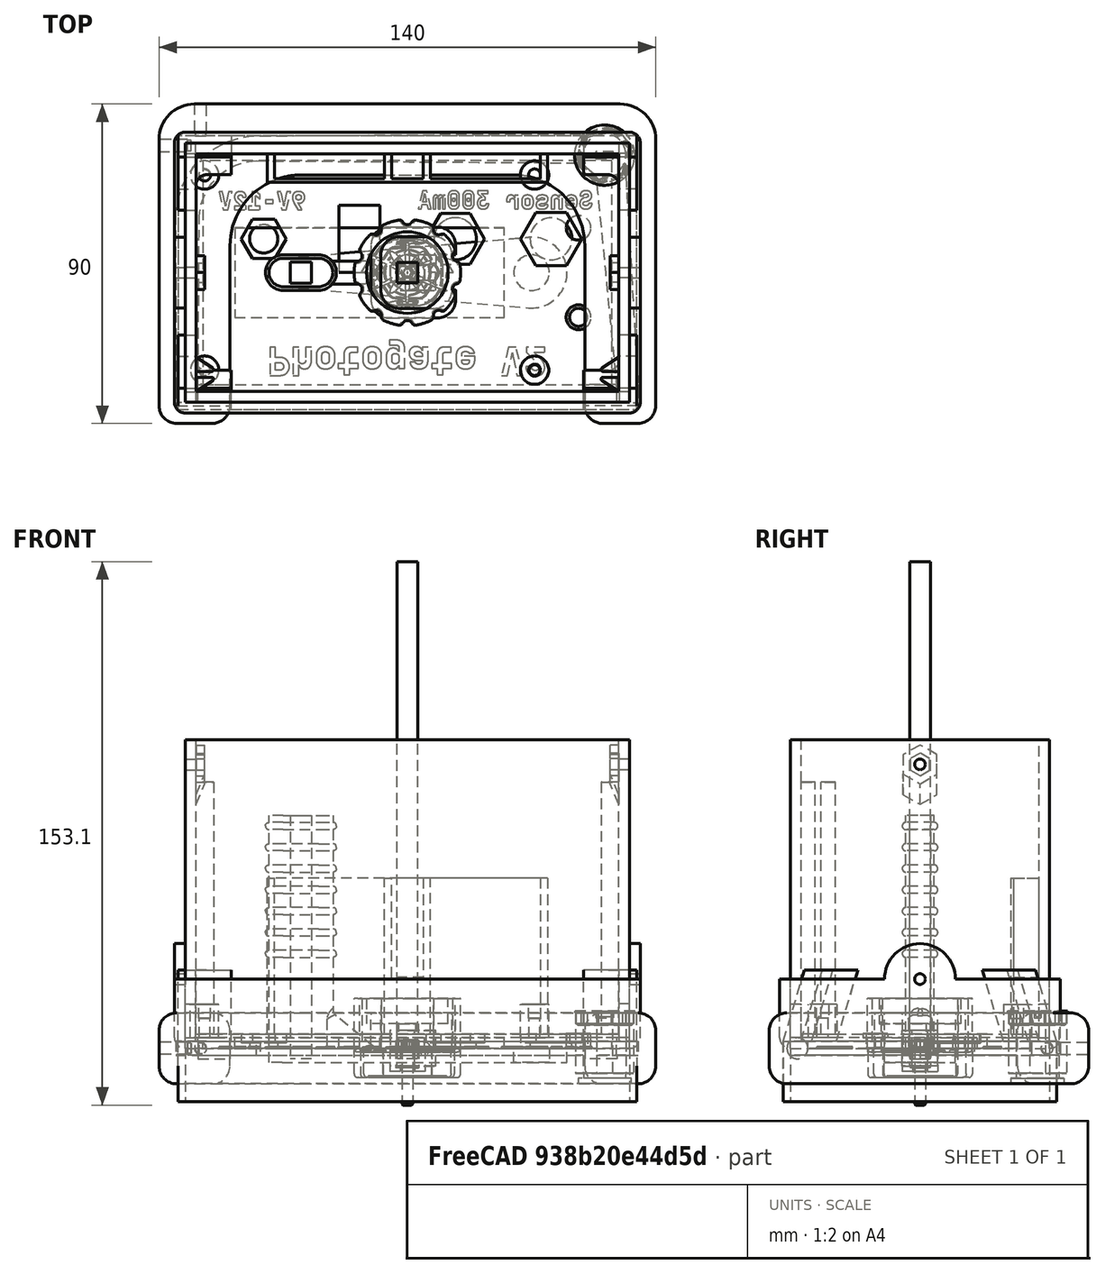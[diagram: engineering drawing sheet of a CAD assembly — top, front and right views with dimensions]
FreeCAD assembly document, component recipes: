
FREECAD ASSEMBLY — COMPONENT RECIPES ("All_Models")

This assembly document has 21 components, labeled P0..P20 below (a component is one placed body or linked part). 17 of them carry a construction recipe — the FreeCAD feature program that regenerates the part from scratch, quoted from this document or its linked companion documents; the rest are supplied as boundary geometry only. No exploded tour is included for this assembly.
NOTE — document 2 of 2 of this assembly tour. The two overview renders and the header above are repeated from document 1; the component sections below continue where the previous document stopped.
COMPONENT P18 — recipe-attached ("ThumbScrew001", modeled in this document).
Construction recipe (the document's own serialized feature program — sketch geometry with constraints, then the solid features built on it; lengths are millimeters unless a unit is written):

FEATURE [Sketcher::SketchObject] Sketch012
  ArcFitTolerance = 1e-06
  AttachmentSupport = -> [XY_Plane003]
  ExternalTypes = [0]
  FullyConstrained = true
  MakeInternals = false
  MapMode = 5
  _ExternalGeoVersion = 0
  sketch-geometry (1):
    g0: Circle CenterX=0 CenterY=0 CenterZ=0 NormalX=0 NormalY=0 NormalZ=1 AngleXU=0 Radius=15
  constraints (2):
    c: Diameter(g0) = 30
    c: Coincident(g0,g-1)
FEATURE [PartDesign::Pad] Pad012
  Direction = (0,0,1)
  Length = 8.2
  Length2 = 10
  Profile = -> Sketch012
  ReferenceAxis = -> Sketch012 [N_Axis]
  Refine = true
  Reversed = true
  SideType = 0
  Suppressed = false
  Type = 0
  Type2 = 0
FEATURE [Sketcher::SketchObject] Sketch013
  ArcFitTolerance = 1e-06
  AttachmentSupport = -> [XY_Plane003]
  ExternalGeometry = -> [Pad012]
  ExternalTypes = [0]
  FullyConstrained = true
  MakeInternals = false
  MapMode = 5
  _ExternalGeoVersion = 0
  sketch-geometry (4):
    g0: LineSegment [constr] StartX=0 StartY=0 StartZ=0 EndX=-1.95789 EndY=14.8717 EndZ=0
    g1: LineSegment [constr] StartX=0 StartY=0 StartZ=0 EndX=1.95789 EndY=14.8717 EndZ=0
    g2: ArcOfCircle CenterX=0 CenterY=0 CenterZ=0 NormalX=0 NormalY=0 NormalZ=1 AngleXU=0 Radius=15 StartAngle=1.4399 EndAngle=1.7017
    g3: ArcOfCircle CenterX=-4.3e-15 CenterY=15 CenterZ=0 NormalX=0 NormalY=0 NormalZ=1 AngleXU=0 Radius=1.96209 StartAngle=3.20704 EndAngle=6.21774
  constraints (12):
    c: PointOnObject(g0,g-3)
    c: PointOnObject(g1,g-3)
    c: Horizontal(g1,g0)
    c: Coincident(g1,g-1)
    c: Coincident(g0,g1)
    c: PointOnObject(g3,g2)
    c: Coincident(g3,g2)
    c: Coincident(g3,g2)
    c: Coincident(g2,g0)
    c: Horizontal(g0,g2)
    c: Coincident(g2,g0)
    c: Angle(g1,g0) = 0.261799
FEATURE [PartDesign::Pocket] Pocket011
  BaseFeature = -> Pad012
  Direction = (0,0,-1)
  Length = 5
  Length2 = 5
  Profile = -> Sketch013
  ReferenceAxis = -> Sketch013 [N_Axis]
  Refine = true
  SideType = 0
  Suppressed = false
  Type = 1
  Type2 = 0
FEATURE [PartDesign::PolarPattern] PolarPattern
  Angle = 360
  Axis = -> Sketch013 [N_Axis]
  BaseFeature = -> Pocket011
  Mode = 0
  Occurrences = 10
  Offset = 120
  Originals = -> [Pocket011]
  Refine = true
  SpacingPattern = [0]
  Spacings = [-1,-1,-1,-1,-1,-1,-1,-1,-1]
  Suppressed = false
  TransformMode = 0
FEATURE [PartDesign::Fillet] Fillet002
  Base = -> PolarPattern [Face22,Face11,Face9,Face7,Face5,Face3,Face21,Face19,Face17,Face15,Face13]
  BaseFeature = -> PolarPattern
  Radius = 1
  Refine = true
  SupportTransform = false
  Suppressed = false
  UseAllEdges = false
FEATURE [Sketcher::SketchObject] Sketch015
  ArcFitTolerance = 1e-06
  AttachmentSupport = -> [Fillet002]
  ExternalTypes = [0]
  FullyConstrained = true
  MakeInternals = false
  MapMode = 5
  _ExternalGeoVersion = 0
  sketch-geometry (9):
    g0: Circle CenterX=0 CenterY=0 CenterZ=0 NormalX=0 NormalY=0 NormalZ=1 AngleXU=0 Radius=4.85
    g1: Circle CenterX=0 CenterY=0 CenterZ=0 NormalX=0 NormalY=0 NormalZ=1 AngleXU=0 Radius=2.75
    g2: LineSegment StartX=2.6 StartY=1.50111 StartZ=0 EndX=4.237e-13 EndY=3.00222 EndZ=0
    g3: LineSegment StartX=4.237e-13 StartY=3.00222 StartZ=0 EndX=-2.6 EndY=1.50111 EndZ=0
    g4: LineSegment StartX=-2.6 StartY=1.50111 StartZ=0 EndX=-2.6 EndY=-1.50111 EndZ=0
    g5: LineSegment StartX=-2.6 StartY=-1.50111 StartZ=0 EndX=1.88329e-11 EndY=-3.00222 EndZ=0
    g6: LineSegment StartX=1.88329e-11 StartY=-3.00222 StartZ=0 EndX=2.6 EndY=-1.50111 EndZ=0
    g7: LineSegment StartX=2.6 StartY=-1.50111 StartZ=0 EndX=2.6 EndY=1.50111 EndZ=0
    g8: Circle [constr] CenterX=0 CenterY=0 CenterZ=0 NormalX=0 NormalY=0 NormalZ=1 AngleXU=0 Radius=3.00222
  constraints (20):
    c: Diameter(g0) = 9.7
    c: Coincident(g0,g-1)
    c: Diameter(g1) = 5.5
    c: Coincident(g1,g0)
    c: Coincident(g2,g3)
    c: Coincident(g3,g4)
    c: Coincident(g4,g5)
    c: Coincident(g5,g6)
    c: Coincident(g6,g7)
    c: Coincident(g7,g2)
    c: Equal(g2, g3-g7) x5
    c: PointOnObject(g2,g8)
    c: PointOnObject(g3,g8)
    c: PointOnObject(g4,g8)
    c: PointOnObject(g5,g8)
    c: PointOnObject(g6,g8)
    c: PointOnObject(g7,g8)
    c: Coincident(g8,g0)
    c: Horizontal(g3,g2)
    c: DistanceX(g3,g2) = 5.2
FEATURE [PartDesign::Pocket] Pocket012
  BaseFeature = -> Fillet002
  Direction = (0,0,-1)
  Length = 3
  Length2 = 5
  Profile = -> Sketch015 [Edge2]
  ReferenceAxis = -> Sketch015 [N_Axis]
  Refine = true
  SideType = 0
  Suppressed = false
  Type = 0
  Type2 = 0
FEATURE [PartDesign::Pad] Pad032
  BaseFeature = -> Pocket012
  Direction = (0,0,1)
  Length = 4
  Length2 = 10
  Profile = -> Sketch015 [Edge1,Edge6,Edge5,Edge7,Edge8,Edge3,Edge4]
  ReferenceAxis = -> Sketch015 [N_Axis]
  Refine = true
  SideType = 0
  Suppressed = false
  Type = 0
  Type2 = 0
FEATURE [Sketcher::SketchObject] Sketch050  label="LorxiSymbol"
  ArcFitTolerance = 1e-06
  AttachmentOffset = pos=(11,-9.424,0) rot=(0,0,1;0rad)
  AttachmentSupport = -> [Pad032]
  ExternalTypes = [0]
  FullyConstrained = false
  MakeInternals = false
  MapMode = 5
  Placement = pos=(11,9.424,-8.2) rot=(1,0,0;3.14159rad)
  _ExternalGeoVersion = 0
  sketch-geometry (292):
    g0: BSplineCurve PolesCount=4 KnotsCount=2 Degree=3 IsPeriodic=0
    g1: BSplineCurve PolesCount=2 KnotsCount=2 Degree=1 IsPeriodic=0
    g2: BSplineCurve PolesCount=2 KnotsCount=2 Degree=1 IsPeriodic=0
    g3: BSplineCurve PolesCount=2 KnotsCount=2 Degree=1 IsPeriodic=0
    g4: BSplineCurve PolesCount=4 KnotsCount=2 Degree=3 IsPeriodic=0
    g5: BSplineCurve PolesCount=4 KnotsCount=2 Degree=3 IsPeriodic=0
    g6: BSplineCurve PolesCount=2 KnotsCount=2 Degree=1 IsPeriodic=0
    g7: BSplineCurve PolesCount=2 KnotsCount=2 Degree=1 IsPeriodic=0
    g8: BSplineCurve PolesCount=2 KnotsCount=2 Degree=1 IsPeriodic=0
    g9: BSplineCurve PolesCount=4 KnotsCount=2 Degree=3 IsPeriodic=0
    g10: BSplineCurve PolesCount=2 KnotsCount=2 Degree=1 IsPeriodic=0
    g11: BSplineCurve PolesCount=2 KnotsCount=2 Degree=1 IsPeriodic=0
    g12: BSplineCurve PolesCount=4 KnotsCount=2 Degree=3 IsPeriodic=0
    g13: BSplineCurve PolesCount=4 KnotsCount=2 Degree=3 IsPeriodic=0
    g14: BSplineCurve PolesCount=2 KnotsCount=2 Degree=1 IsPeriodic=0
    g15: BSplineCurve PolesCount=2 KnotsCount=2 Degree=1 IsPeriodic=0
    g16: BSplineCurve PolesCount=2 KnotsCount=2 Degree=1 IsPeriodic=0
    g17: BSplineCurve PolesCount=4 KnotsCount=2 Degree=3 IsPeriodic=0
    g18: BSplineCurve PolesCount=2 KnotsCount=2 Degree=1 IsPeriodic=0
    g19: BSplineCurve PolesCount=4 KnotsCount=2 Degree=3 IsPeriodic=0
    g20: BSplineCurve PolesCount=4 KnotsCount=2 Degree=3 IsPeriodic=0
    g21: BSplineCurve PolesCount=2 KnotsCount=2 Degree=1 IsPeriodic=0
    g22: BSplineCurve PolesCount=4 KnotsCount=2 Degree=3 IsPeriodic=0
    g23: BSplineCurve PolesCount=4 KnotsCount=2 Degree=3 IsPeriodic=0
    g24: BSplineCurve PolesCount=2 KnotsCount=2 Degree=1 IsPeriodic=0
    g25: BSplineCurve PolesCount=4 KnotsCount=2 Degree=3 IsPeriodic=0
    g26: BSplineCurve PolesCount=4 KnotsCount=2 Degree=3 IsPeriodic=0
    g27: BSplineCurve PolesCount=2 KnotsCount=2 Degree=1 IsPeriodic=0
    g28: BSplineCurve PolesCount=4 KnotsCount=2 Degree=3 IsPeriodic=0
    g29: BSplineCurve PolesCount=4 KnotsCount=2 Degree=3 IsPeriodic=0
    g30: BSplineCurve PolesCount=2 KnotsCount=2 Degree=1 IsPeriodic=0
    g31: BSplineCurve PolesCount=4 KnotsCount=2 Degree=3 IsPeriodic=0
    g32: BSplineCurve PolesCount=4 KnotsCount=2 Degree=3 IsPeriodic=0
    g33: BSplineCurve PolesCount=2 KnotsCount=2 Degree=1 IsPeriodic=0
    g34: BSplineCurve PolesCount=4 KnotsCount=2 Degree=3 IsPeriodic=0
    g35: BSplineCurve PolesCount=4 KnotsCount=2 Degree=3 IsPeriodic=0
    g36: BSplineCurve PolesCount=2 KnotsCount=2 Degree=1 IsPeriodic=0
    g37: BSplineCurve PolesCount=4 KnotsCount=2 Degree=3 IsPeriodic=0
    g38: BSplineCurve PolesCount=4 KnotsCount=2 Degree=3 IsPeriodic=0
    g39: BSplineCurve PolesCount=4 KnotsCount=2 Degree=3 IsPeriodic=0
    g40: BSplineCurve PolesCount=4 KnotsCount=2 Degree=3 IsPeriodic=0
    g41: BSplineCurve PolesCount=2 KnotsCount=2 Degree=1 IsPeriodic=0
    g42: BSplineCurve PolesCount=4 KnotsCount=2 Degree=3 IsPeriodic=0
    g43: BSplineCurve PolesCount=4 KnotsCount=2 Degree=3 IsPeriodic=0
    g44: BSplineCurve PolesCount=4 KnotsCount=2 Degree=3 IsPeriodic=0
    g45: BSplineCurve PolesCount=4 KnotsCount=2 Degree=3 IsPeriodic=0
    g46: BSplineCurve PolesCount=2 KnotsCount=2 Degree=1 IsPeriodic=0
    g47: BSplineCurve PolesCount=4 KnotsCount=2 Degree=3 IsPeriodic=0
    g48: BSplineCurve PolesCount=4 KnotsCount=2 Degree=3 IsPeriodic=0
    g49: BSplineCurve PolesCount=4 KnotsCount=2 Degree=3 IsPeriodic=0
    g50: BSplineCurve PolesCount=2 KnotsCount=2 Degree=1 IsPeriodic=0
    g51: BSplineCurve PolesCount=2 KnotsCount=2 Degree=1 IsPeriodic=0
    g52: BSplineCurve PolesCount=4 KnotsCount=2 Degree=3 IsPeriodic=0
    g53: BSplineCurve PolesCount=2 KnotsCount=2 Degree=1 IsPeriodic=0
    g54: BSplineCurve PolesCount=2 KnotsCount=2 Degree=1 IsPeriodic=0
    g55: BSplineCurve PolesCount=2 KnotsCount=2 Degree=1 IsPeriodic=0
    g56: BSplineCurve PolesCount=4 KnotsCount=2 Degree=3 IsPeriodic=0
    g57: BSplineCurve PolesCount=2 KnotsCount=2 Degree=1 IsPeriodic=0
    g58: BSplineCurve PolesCount=2 KnotsCount=2 Degree=1 IsPeriodic=0
    g59: BSplineCurve PolesCount=4 KnotsCount=2 Degree=3 IsPeriodic=0
    g60: BSplineCurve PolesCount=4 KnotsCount=2 Degree=3 IsPeriodic=0
    g61: BSplineCurve PolesCount=4 KnotsCount=2 Degree=3 IsPeriodic=0
    g62: BSplineCurve PolesCount=4 KnotsCount=2 Degree=3 IsPeriodic=0
    g63: BSplineCurve PolesCount=4 KnotsCount=2 Degree=3 IsPeriodic=0
    g64: BSplineCurve PolesCount=4 KnotsCount=2 Degree=3 IsPeriodic=0
    g65: BSplineCurve PolesCount=2 KnotsCount=2 Degree=1 IsPeriodic=0
    g66: BSplineCurve PolesCount=4 KnotsCount=2 Degree=3 IsPeriodic=0
    g67: BSplineCurve PolesCount=4 KnotsCount=2 Degree=3 IsPeriodic=0
    g68: BSplineCurve PolesCount=2 KnotsCount=2 Degree=1 IsPeriodic=0
    g69: BSplineCurve PolesCount=4 KnotsCount=2 Degree=3 IsPeriodic=0
    g70: BSplineCurve PolesCount=4 KnotsCount=2 Degree=3 IsPeriodic=0
    g71: BSplineCurve PolesCount=4 KnotsCount=2 Degree=3 IsPeriodic=0
    g72: BSplineCurve PolesCount=4 KnotsCount=2 Degree=3 IsPeriodic=0
    g73: BSplineCurve PolesCount=4 KnotsCount=2 Degree=3 IsPeriodic=0
    g74: BSplineCurve PolesCount=2 KnotsCount=2 Degree=1 IsPeriodic=0
    g75: BSplineCurve PolesCount=2 KnotsCount=2 Degree=1 IsPeriodic=0
    g76: BSplineCurve PolesCount=4 KnotsCount=2 Degree=3 IsPeriodic=0
    g77: BSplineCurve PolesCount=4 KnotsCount=2 Degree=3 IsPeriodic=0
    g78: BSplineCurve PolesCount=4 KnotsCount=2 Degree=3 IsPeriodic=0
    g79: BSplineCurve PolesCount=4 KnotsCount=2 Degree=3 IsPeriodic=0
    g80: BSplineCurve PolesCount=4 KnotsCount=2 Degree=3 IsPeriodic=0
    g81: BSplineCurve PolesCount=2 KnotsCount=2 Degree=1 IsPeriodic=0
    g82: BSplineCurve PolesCount=4 KnotsCount=2 Degree=3 IsPeriodic=0
    g83: BSplineCurve PolesCount=4 KnotsCount=2 Degree=3 IsPeriodic=0
    g84: BSplineCurve PolesCount=2 KnotsCount=2 Degree=1 IsPeriodic=0
    g85: BSplineCurve PolesCount=4 KnotsCount=2 Degree=3 IsPeriodic=0
    g86: BSplineCurve PolesCount=4 KnotsCount=2 Degree=3 IsPeriodic=0
    g87: BSplineCurve PolesCount=4 KnotsCount=2 Degree=3 IsPeriodic=0
    g88: BSplineCurve PolesCount=4 KnotsCount=2 Degree=3 IsPeriodic=0
    g89: BSplineCurve PolesCount=4 KnotsCount=2 Degree=3 IsPeriodic=0
    g90: BSplineCurve PolesCount=4 KnotsCount=2 Degree=3 IsPeriodic=0
    g91: BSplineCurve PolesCount=2 KnotsCount=2 Degree=1 IsPeriodic=0
    g92: BSplineCurve PolesCount=2 KnotsCount=2 Degree=1 IsPeriodic=0
    g93: BSplineCurve PolesCount=4 KnotsCount=2 Degree=3 IsPeriodic=0
    g94: BSplineCurve PolesCount=2 KnotsCount=2 Degree=1 IsPeriodic=0
    g95: BSplineCurve PolesCount=2 KnotsCount=2 Degree=1 IsPeriodic=0
    g96: BSplineCurve PolesCount=2 KnotsCount=2 Degree=1 IsPeriodic=0
    g97: BSplineCurve PolesCount=4 KnotsCount=2 Degree=3 IsPeriodic=0
    g98: BSplineCurve PolesCount=2 KnotsCount=2 Degree=1 IsPeriodic=0
    g99: BSplineCurve PolesCount=2 KnotsCount=2 Degree=1 IsPeriodic=0
    g100: BSplineCurve PolesCount=4 KnotsCount=2 Degree=3 IsPeriodic=0
    g101: BSplineCurve PolesCount=4 KnotsCount=2 Degree=3 IsPeriodic=0
    g102: BSplineCurve PolesCount=4 KnotsCount=2 Degree=3 IsPeriodic=0
    g103: BSplineCurve PolesCount=4 KnotsCount=2 Degree=3 IsPeriodic=0
    g104: BSplineCurve PolesCount=2 KnotsCount=2 Degree=1 IsPeriodic=0
    g105: BSplineCurve PolesCount=4 KnotsCount=2 Degree=3 IsPeriodic=0
    g106: BSplineCurve PolesCount=4 KnotsCount=2 Degree=3 IsPeriodic=0
    g107: BSplineCurve PolesCount=4 KnotsCount=2 Degree=3 IsPeriodic=0
    g108: BSplineCurve PolesCount=2 KnotsCount=2 Degree=1 IsPeriodic=0
    g109: BSplineCurve PolesCount=4 KnotsCount=2 Degree=3 IsPeriodic=0
    g110: BSplineCurve PolesCount=4 KnotsCount=2 Degree=3 IsPeriodic=0
    g111: BSplineCurve PolesCount=2 KnotsCount=2 Degree=1 IsPeriodic=0
    g112: BSplineCurve PolesCount=4 KnotsCount=2 Degree=3 IsPeriodic=0
    g113: BSplineCurve PolesCount=4 KnotsCount=2 Degree=3 IsPeriodic=0
    g114: BSplineCurve PolesCount=4 KnotsCount=2 Degree=3 IsPeriodic=0
    g115: BSplineCurve PolesCount=2 KnotsCount=2 Degree=1 IsPeriodic=0
    g116: BSplineCurve PolesCount=4 KnotsCount=2 Degree=3 IsPeriodic=0
    g117: BSplineCurve PolesCount=2 KnotsCount=2 Degree=1 IsPeriodic=0
    g118: BSplineCurve PolesCount=4 KnotsCount=2 Degree=3 IsPeriodic=0
    g119: BSplineCurve PolesCount=2 KnotsCount=2 Degree=1 IsPeriodic=0
    g120: BSplineCurve PolesCount=4 KnotsCount=2 Degree=3 IsPeriodic=0
    g121: BSplineCurve PolesCount=2 KnotsCount=2 Degree=1 IsPeriodic=0
    g122: BSplineCurve PolesCount=4 KnotsCount=2 Degree=3 IsPeriodic=0
    g123: BSplineCurve PolesCount=2 KnotsCount=2 Degree=1 IsPeriodic=0
    g124: BSplineCurve PolesCount=4 KnotsCount=2 Degree=3 IsPeriodic=0
    g125: BSplineCurve PolesCount=4 KnotsCount=2 Degree=3 IsPeriodic=0
    g126: BSplineCurve PolesCount=4 KnotsCount=2 Degree=3 IsPeriodic=0
    g127: BSplineCurve PolesCount=2 KnotsCount=2 Degree=1 IsPeriodic=0
    g128: BSplineCurve PolesCount=4 KnotsCount=2 Degree=3 IsPeriodic=0
    g129: BSplineCurve PolesCount=4 KnotsCount=2 Degree=3 IsPeriodic=0
    g130: BSplineCurve PolesCount=2 KnotsCount=2 Degree=1 IsPeriodic=0
    g131: BSplineCurve PolesCount=4 KnotsCount=2 Degree=3 IsPeriodic=0
    g132: BSplineCurve PolesCount=4 KnotsCount=2 Degree=3 IsPeriodic=0
    g133: BSplineCurve PolesCount=4 KnotsCount=2 Degree=3 IsPeriodic=0
    g134: BSplineCurve PolesCount=4 KnotsCount=2 Degree=3 IsPeriodic=0
    g135: BSplineCurve PolesCount=2 KnotsCount=2 Degree=1 IsPeriodic=0
    g136: BSplineCurve PolesCount=4 KnotsCount=2 Degree=3 IsPeriodic=0
    g137: BSplineCurve PolesCount=4 KnotsCount=2 Degree=3 IsPeriodic=0
    g138: BSplineCurve PolesCount=4 KnotsCount=2 Degree=3 IsPeriodic=0
    g139: BSplineCurve PolesCount=4 KnotsCount=2 Degree=3 IsPeriodic=0
    g140: BSplineCurve PolesCount=2 KnotsCount=2 Degree=1 IsPeriodic=0
    g141: BSplineCurve PolesCount=4 KnotsCount=2 Degree=3 IsPeriodic=0
    g142: BSplineCurve PolesCount=4 KnotsCount=2 Degree=3 IsPeriodic=0
    g143: BSplineCurve PolesCount=4 KnotsCount=2 Degree=3 IsPeriodic=0
    g144: BSplineCurve PolesCount=2 KnotsCount=2 Degree=1 IsPeriodic=0
    g145: BSplineCurve PolesCount=2 KnotsCount=2 Degree=1 IsPeriodic=0
    g146: BSplineCurve PolesCount=4 KnotsCount=2 Degree=3 IsPeriodic=0
    g147: BSplineCurve PolesCount=2 KnotsCount=2 Degree=1 IsPeriodic=0
    g148: BSplineCurve PolesCount=2 KnotsCount=2 Degree=1 IsPeriodic=0
    g149: BSplineCurve PolesCount=2 KnotsCount=2 Degree=1 IsPeriodic=0
    g150: BSplineCurve PolesCount=4 KnotsCount=2 Degree=3 IsPeriodic=0
    g151: BSplineCurve PolesCount=2 KnotsCount=2 Degree=1 IsPeriodic=0
    g152: BSplineCurve PolesCount=2 KnotsCount=2 Degree=1 IsPeriodic=0
    g153: BSplineCurve PolesCount=4 KnotsCount=2 Degree=3 IsPeriodic=0
    g154: BSplineCurve PolesCount=4 KnotsCount=2 Degree=3 IsPeriodic=0
    g155: BSplineCurve PolesCount=4 KnotsCount=2 Degree=3 IsPeriodic=0
    g156: BSplineCurve PolesCount=4 KnotsCount=2 Degree=3 IsPeriodic=0
    g157: BSplineCurve PolesCount=4 KnotsCount=2 Degree=3 IsPeriodic=0
    g158: BSplineCurve PolesCount=2 KnotsCount=2 Degree=1 IsPeriodic=0
    g159: BSplineCurve PolesCount=4 KnotsCount=2 Degree=3 IsPeriodic=0
    g160: BSplineCurve PolesCount=4 KnotsCount=2 Degree=3 IsPeriodic=0
    g161: BSplineCurve PolesCount=2 KnotsCount=2 Degree=1 IsPeriodic=0
    g162: BSplineCurve PolesCount=4 KnotsCount=2 Degree=3 IsPeriodic=0
    g163: BSplineCurve PolesCount=4 KnotsCount=2 Degree=3 IsPeriodic=0
    g164: BSplineCurve PolesCount=4 KnotsCount=2 Degree=3 IsPeriodic=0
    g165: BSplineCurve PolesCount=4 KnotsCount=2 Degree=3 IsPeriodic=0
    g166: BSplineCurve PolesCount=4 KnotsCount=2 Degree=3 IsPeriodic=0
    g167: BSplineCurve PolesCount=2 KnotsCount=2 Degree=1 IsPeriodic=0
    g168: BSplineCurve PolesCount=2 KnotsCount=2 Degree=1 IsPeriodic=0
    g169: BSplineCurve PolesCount=4 KnotsCount=2 Degree=3 IsPeriodic=0
    g170: BSplineCurve PolesCount=4 KnotsCount=2 Degree=3 IsPeriodic=0
    g171: BSplineCurve PolesCount=4 KnotsCount=2 Degree=3 IsPeriodic=0
    g172: BSplineCurve PolesCount=4 KnotsCount=2 Degree=3 IsPeriodic=0
    g173: BSplineCurve PolesCount=4 KnotsCount=2 Degree=3 IsPeriodic=0
    g174: BSplineCurve PolesCount=2 KnotsCount=2 Degree=1 IsPeriodic=0
    g175: BSplineCurve PolesCount=4 KnotsCount=2 Degree=3 IsPeriodic=0
    g176: BSplineCurve PolesCount=4 KnotsCount=2 Degree=3 IsPeriodic=0
    g177: BSplineCurve PolesCount=2 KnotsCount=2 Degree=1 IsPeriodic=0
    g178: BSplineCurve PolesCount=4 KnotsCount=2 Degree=3 IsPeriodic=0
    g179: BSplineCurve PolesCount=4 KnotsCount=2 Degree=3 IsPeriodic=0
    g180: BSplineCurve PolesCount=4 KnotsCount=2 Degree=3 IsPeriodic=0
    g181: BSplineCurve PolesCount=4 KnotsCount=2 Degree=3 IsPeriodic=0
    g182: BSplineCurve PolesCount=4 KnotsCount=2 Degree=3 IsPeriodic=0
    g183: BSplineCurve PolesCount=2 KnotsCount=2 Degree=1 IsPeriodic=0
    g184: BSplineCurve PolesCount=2 KnotsCount=2 Degree=1 IsPeriodic=0
    g185: BSplineCurve PolesCount=4 KnotsCount=2 Degree=3 IsPeriodic=0
    g186: BSplineCurve PolesCount=2 KnotsCount=2 Degree=1 IsPeriodic=0
    g187: BSplineCurve PolesCount=2 KnotsCount=2 Degree=1 IsPeriodic=0
    g188: BSplineCurve PolesCount=2 KnotsCount=2 Degree=1 IsPeriodic=0
    g189: BSplineCurve PolesCount=4 KnotsCount=2 Degree=3 IsPeriodic=0
    g190: BSplineCurve PolesCount=2 KnotsCount=2 Degree=1 IsPeriodic=0
    g191: BSplineCurve PolesCount=2 KnotsCount=2 Degree=1 IsPeriodic=0
    g192: BSplineCurve PolesCount=4 KnotsCount=2 Degree=3 IsPeriodic=0
    g193: BSplineCurve PolesCount=4 KnotsCount=2 Degree=3 IsPeriodic=0
    g194: BSplineCurve PolesCount=4 KnotsCount=2 Degree=3 IsPeriodic=0
    g195: BSplineCurve PolesCount=4 KnotsCount=2 Degree=3 IsPeriodic=0
    g196: BSplineCurve PolesCount=2 KnotsCount=2 Degree=1 IsPeriodic=0
    g197: BSplineCurve PolesCount=4 KnotsCount=2 Degree=3 IsPeriodic=0
    g198: BSplineCurve PolesCount=4 KnotsCount=2 Degree=3 IsPeriodic=0
    g199: BSplineCurve PolesCount=4 KnotsCount=2 Degree=3 IsPeriodic=0
    g200: BSplineCurve PolesCount=2 KnotsCount=2 Degree=1 IsPeriodic=0
    g201: BSplineCurve PolesCount=4 KnotsCount=2 Degree=3 IsPeriodic=0
    g202: BSplineCurve PolesCount=4 KnotsCount=2 Degree=3 IsPeriodic=0
    g203: BSplineCurve PolesCount=2 KnotsCount=2 Degree=1 IsPeriodic=0
    g204: BSplineCurve PolesCount=4 KnotsCount=2 Degree=3 IsPeriodic=0
    g205: BSplineCurve PolesCount=4 KnotsCount=2 Degree=3 IsPeriodic=0
    g206: BSplineCurve PolesCount=4 KnotsCount=2 Degree=3 IsPeriodic=0
    g207: BSplineCurve PolesCount=2 KnotsCount=2 Degree=1 IsPeriodic=0
    g208: BSplineCurve PolesCount=4 KnotsCount=2 Degree=3 IsPeriodic=0
    g209: BSplineCurve PolesCount=2 KnotsCount=2 Degree=1 IsPeriodic=0
    g210: BSplineCurve PolesCount=4 KnotsCount=2 Degree=3 IsPeriodic=0
    g211: BSplineCurve PolesCount=2 KnotsCount=2 Degree=1 IsPeriodic=0
    g212: BSplineCurve PolesCount=4 KnotsCount=2 Degree=3 IsPeriodic=0
    g213: BSplineCurve PolesCount=2 KnotsCount=2 Degree=1 IsPeriodic=0
    g214: BSplineCurve PolesCount=4 KnotsCount=2 Degree=3 IsPeriodic=0
    g215: BSplineCurve PolesCount=2 KnotsCount=2 Degree=1 IsPeriodic=0
    g216: BSplineCurve PolesCount=4 KnotsCount=2 Degree=3 IsPeriodic=0
    g217: BSplineCurve PolesCount=4 KnotsCount=2 Degree=3 IsPeriodic=0
    g218: BSplineCurve PolesCount=4 KnotsCount=2 Degree=3 IsPeriodic=0
    g219: BSplineCurve PolesCount=2 KnotsCount=2 Degree=1 IsPeriodic=0
    g220: BSplineCurve PolesCount=2 KnotsCount=2 Degree=1 IsPeriodic=0
    g221: BSplineCurve PolesCount=4 KnotsCount=2 Degree=3 IsPeriodic=0
    g222: BSplineCurve PolesCount=4 KnotsCount=2 Degree=3 IsPeriodic=0
    g223: BSplineCurve PolesCount=4 KnotsCount=2 Degree=3 IsPeriodic=0
    g224: BSplineCurve PolesCount=4 KnotsCount=2 Degree=3 IsPeriodic=0
    g225: BSplineCurve PolesCount=4 KnotsCount=2 Degree=3 IsPeriodic=0
    g226: BSplineCurve PolesCount=4 KnotsCount=2 Degree=3 IsPeriodic=0
    g227: BSplineCurve PolesCount=2 KnotsCount=2 Degree=1 IsPeriodic=0
    g228: BSplineCurve PolesCount=2 KnotsCount=2 Degree=1 IsPeriodic=0
    g229: BSplineCurve PolesCount=4 KnotsCount=2 Degree=3 IsPeriodic=0
    g230: BSplineCurve PolesCount=4 KnotsCount=2 Degree=3 IsPeriodic=0
    g231: BSplineCurve PolesCount=4 KnotsCount=2 Degree=3 IsPeriodic=0
    g232: BSplineCurve PolesCount=2 KnotsCount=2 Degree=1 IsPeriodic=0
    g233: BSplineCurve PolesCount=2 KnotsCount=2 Degree=1 IsPeriodic=0
    g234: BSplineCurve PolesCount=2 KnotsCount=2 Degree=1 IsPeriodic=0
    g235: BSplineCurve PolesCount=2 KnotsCount=2 Degree=1 IsPeriodic=0
    g236: BSplineCurve PolesCount=2 KnotsCount=2 Degree=1 IsPeriodic=0
    g237: BSplineCurve PolesCount=4 KnotsCount=2 Degree=3 IsPeriodic=0
    g238: BSplineCurve PolesCount=4 KnotsCount=2 Degree=3 IsPeriodic=0
    g239: BSplineCurve PolesCount=4 KnotsCount=2 Degree=3 IsPeriodic=0
    g240: BSplineCurve PolesCount=4 KnotsCount=2 Degree=3 IsPeriodic=0
    g241: BSplineCurve PolesCount=4 KnotsCount=2 Degree=3 IsPeriodic=0
    g242: BSplineCurve PolesCount=4 KnotsCount=2 Degree=3 IsPeriodic=0
    g243: BSplineCurve PolesCount=4 KnotsCount=2 Degree=3 IsPeriodic=0
    g244: BSplineCurve PolesCount=4 KnotsCount=2 Degree=3 IsPeriodic=0
    g245: BSplineCurve PolesCount=2 KnotsCount=2 Degree=1 IsPeriodic=0
    g246: BSplineCurve PolesCount=2 KnotsCount=2 Degree=1 IsPeriodic=0
    g247: BSplineCurve PolesCount=4 KnotsCount=2 Degree=3 IsPeriodic=0
    g248: BSplineCurve PolesCount=4 KnotsCount=2 Degree=3 IsPeriodic=0
    g249: BSplineCurve PolesCount=4 KnotsCount=2 Degree=3 IsPeriodic=0
    g250: BSplineCurve PolesCount=4 KnotsCount=2 Degree=3 IsPeriodic=0
    g251: BSplineCurve PolesCount=4 KnotsCount=2 Degree=3 IsPeriodic=0
    g252: BSplineCurve PolesCount=4 KnotsCount=2 Degree=3 IsPeriodic=0
    g253: BSplineCurve PolesCount=2 KnotsCount=2 Degree=1 IsPeriodic=0
    g254: BSplineCurve PolesCount=4 KnotsCount=2 Degree=3 IsPeriodic=0
    g255: BSplineCurve PolesCount=2 KnotsCount=2 Degree=1 IsPeriodic=0
    g256: BSplineCurve PolesCount=4 KnotsCount=2 Degree=3 IsPeriodic=0
    g257: BSplineCurve PolesCount=2 KnotsCount=2 Degree=1 IsPeriodic=0
    g258: BSplineCurve PolesCount=4 KnotsCount=2 Degree=3 IsPeriodic=0
    g259: BSplineCurve PolesCount=2 KnotsCount=2 Degree=1 IsPeriodic=0
    g260: BSplineCurve PolesCount=4 KnotsCount=2 Degree=3 IsPeriodic=0
    g261: BSplineCurve PolesCount=2 KnotsCount=2 Degree=1 IsPeriodic=0
    g262: BSplineCurve PolesCount=4 KnotsCount=2 Degree=3 IsPeriodic=0
    g263: BSplineCurve PolesCount=2 KnotsCount=2 Degree=1 IsPeriodic=0
    g264: BSplineCurve PolesCount=2 KnotsCount=2 Degree=1 IsPeriodic=0
    g265: BSplineCurve PolesCount=4 KnotsCount=2 Degree=3 IsPeriodic=0
    g266: BSplineCurve PolesCount=2 KnotsCount=2 Degree=1 IsPeriodic=0
    g267: BSplineCurve PolesCount=2 KnotsCount=2 Degree=1 IsPeriodic=0
    g268: BSplineCurve PolesCount=4 KnotsCount=2 Degree=3 IsPeriodic=0
    g269: BSplineCurve PolesCount=2 KnotsCount=2 Degree=1 IsPeriodic=0
    g270: BSplineCurve PolesCount=4 KnotsCount=2 Degree=3 IsPeriodic=0
    g271: BSplineCurve PolesCount=2 KnotsCount=2 Degree=1 IsPeriodic=0
    g272: BSplineCurve PolesCount=4 KnotsCount=2 Degree=3 IsPeriodic=0
    g273: BSplineCurve PolesCount=2 KnotsCount=2 Degree=1 IsPeriodic=0
    g274: BSplineCurve PolesCount=4 KnotsCount=2 Degree=3 IsPeriodic=0
    g275: BSplineCurve PolesCount=2 KnotsCount=2 Degree=1 IsPeriodic=0
    g276: BSplineCurve PolesCount=4 KnotsCount=2 Degree=3 IsPeriodic=0
    g277: BSplineCurve PolesCount=2 KnotsCount=2 Degree=1 IsPeriodic=0
    g278: BSplineCurve PolesCount=2 KnotsCount=2 Degree=1 IsPeriodic=0
    g279: BSplineCurve PolesCount=2 KnotsCount=2 Degree=1 IsPeriodic=0
    g280: BSplineCurve PolesCount=2 KnotsCount=2 Degree=1 IsPeriodic=0
    g281: BSplineCurve PolesCount=2 KnotsCount=2 Degree=1 IsPeriodic=0
    g282: BSplineCurve PolesCount=2 KnotsCount=2 Degree=1 IsPeriodic=0
    g283: BSplineCurve PolesCount=2 KnotsCount=2 Degree=1 IsPeriodic=0
    g284: BSplineCurve PolesCount=4 KnotsCount=2 Degree=3 IsPeriodic=0
    g285: BSplineCurve PolesCount=4 KnotsCount=2 Degree=3 IsPeriodic=0
    g286: BSplineCurve PolesCount=4 KnotsCount=2 Degree=3 IsPeriodic=0
    g287: BSplineCurve PolesCount=4 KnotsCount=2 Degree=3 IsPeriodic=0
    g288: BSplineCurve PolesCount=4 KnotsCount=2 Degree=3 IsPeriodic=0
    g289: BSplineCurve PolesCount=4 KnotsCount=2 Degree=3 IsPeriodic=0
    g290: BSplineCurve PolesCount=4 KnotsCount=2 Degree=3 IsPeriodic=0
    g291: BSplineCurve PolesCount=4 KnotsCount=2 Degree=3 IsPeriodic=0
  constraints (292):
    c: Coincident(g0,g1)
    c: Coincident(g1,g2)
    c: Coincident(g2,g3)
    c: Coincident(g3,g4)
    c: Coincident(g4,g5)
    c: Coincident(g5,g6)
    c: Coincident(g6,g7)
    c: Coincident(g7,g8)
    c: Coincident(g8,g9)
    c: Coincident(g9,g0)
    c: Coincident(g10,g11)
    c: Coincident(g11,g12)
    c: Coincident(g12,g13)
    c: Coincident(g13,g14)
    c: Coincident(g14,g15)
    c: Coincident(g15,g16)
    c: Coincident(g16,g17)
    c: Coincident(g17,g18)
    c: Coincident(g18,g10)
    c: Coincident(g19,g20)
    c: Coincident(g20,g21)
    c: Coincident(g21,g22)
    c: Coincident(g22,g23)
    c: Coincident(g23,g24)
    c: Coincident(g24,g19)
    c: Coincident(g25,g26)
    c: Coincident(g26,g27)
    c: Coincident(g27,g28)
    c: Coincident(g28,g29)
    c: Coincident(g29,g30)
    c: Coincident(g30,g25)
    c: Coincident(g31,g32)
    c: Coincident(g32,g33)
    c: Coincident(g33,g34)
    c: Coincident(g34,g35)
    c: Coincident(g35,g36)
    c: Coincident(g36,g37)
    c: Coincident(g37,g38)
    c: Coincident(g38,g31)
    c: Coincident(g39,g40)
    c: Coincident(g40,g41)
    c: Coincident(g41,g42)
    c: Coincident(g42,g39)
    c: Coincident(g43,g44)
    c: Coincident(g44,g45)
    c: Coincident(g45,g46)
    c: Coincident(g46,g43)
    c: Coincident(g47,g48)
    c: Coincident(g48,g49)
    c: Coincident(g49,g50)
    c: Coincident(g50,g51)
    c: Coincident(g51,g52)
    c: Coincident(g52,g53)
    c: Coincident(g53,g54)
    c: Coincident(g54,g55)
    c: Coincident(g55,g56)
    c: Coincident(g56,g57)
    c: Coincident(g57,g58)
    c: Coincident(g58,g59)
    c: Coincident(g59,g60)
    c: Coincident(g60,g61)
    c: Coincident(g61,g62)
    c: Coincident(g62,g63)
    c: Coincident(g63,g64)
    c: Coincident(g64,g65)
    c: Coincident(g65,g66)
    c: Coincident(g66,g67)
    c: Coincident(g67,g68)
    c: Coincident(g68,g69)
    c: Coincident(g69,g70)
    c: Coincident(g70,g71)
    c: Coincident(g71,g72)
    c: Coincident(g72,g73)
    c: Coincident(g73,g74)
    c: Coincident(g74,g75)
    c: Coincident(g75,g76)
    c: Coincident(g76,g77)
    c: Coincident(g77,g78)
    c: Coincident(g78,g79)
    c: Coincident(g79,g80)
    c: Coincident(g80,g81)
    c: Coincident(g81,g82)
    c: Coincident(g82,g83)
    c: Coincident(g83,g84)
    c: Coincident(g84,g85)
    c: Coincident(g85,g86)
    c: Coincident(g86,g87)
    c: Coincident(g87,g88)
    c: Coincident(g88,g89)
    c: Coincident(g89,g90)
    c: Coincident(g90,g91)
    c: Coincident(g91,g92)
    c: Coincident(g92,g93)
    c: Coincident(g93,g94)
    c: Coincident(g94,g95)
    c: Coincident(g95,g96)
    c: Coincident(g96,g97)
    c: Coincident(g97,g98)
    c: Coincident(g98,g99)
    c: Coincident(g99,g100)
    c: Coincident(g100,g101)
    c: Coincident(g101,g102)
    c: Coincident(g102,g103)
    c: Coincident(g103,g104)
    c: Coincident(g104,g105)
    c: Coincident(g105,g106)
    c: Coincident(g106,g107)
    c: Coincident(g107,g108)
    c: Coincident(g108,g109)
    c: Coincident(g109,g110)
    c: Coincident(g110,g111)
    c: Coincident(g111,g112)
    c: Coincident(g112,g113)
    c: Coincident(g113,g114)
    c: Coincident(g114,g115)
    c: Coincident(g115,g116)
    c: Coincident(g116,g47)
    c: Coincident(g117,g118)
    c: Coincident(g118,g119)
    c: Coincident(g119,g120)
    c: Coincident(g120,g121)
    c: Coincident(g121,g122)
    c: Coincident(g122,g123)
    c: Coincident(g123,g124)
    c: Coincident(g124,g117)
    c: Coincident(g125,g126)
    c: Coincident(g126,g127)
    c: Coincident(g127,g128)
    c: Coincident(g128,g129)
    c: Coincident(g129,g130)
    c: Coincident(g130,g131)
    c: Coincident(g131,g132)
    c: Coincident(g132,g125)
    c: Coincident(g133,g134)
    c: Coincident(g134,g135)
    c: Coincident(g135,g136)
    c: Coincident(g136,g133)
    c: Coincident(g137,g138)
    c: Coincident(g138,g139)
    c: Coincident(g139,g140)
    c: Coincident(g140,g137)
    c: Coincident(g141,g142)
    c: Coincident(g142,g143)
    c: Coincident(g143,g144)
    c: Coincident(g144,g145)
    c: Coincident(g145,g146)
    c: Coincident(g146,g147)
    c: Coincident(g147,g148)
    c: Coincident(g148,g149)
    c: Coincident(g149,g150)
    c: Coincident(g150,g151)
    c: Coincident(g151,g152)
    c: Coincident(g152,g153)
    c: Coincident(g153,g154)
    c: Coincident(g154,g155)
    c: Coincident(g155,g156)
    c: Coincident(g156,g157)
    c: Coincident(g157,g158)
    c: Coincident(g158,g159)
    c: Coincident(g159,g160)
    c: Coincident(g160,g161)
    c: Coincident(g161,g162)
    c: Coincident(g162,g163)
    c: Coincident(g163,g164)
    c: Coincident(g164,g165)
    c: Coincident(g165,g166)
    c: Coincident(g166,g167)
    c: Coincident(g167,g168)
    c: Coincident(g168,g169)
    c: Coincident(g169,g170)
    c: Coincident(g170,g171)
    c: Coincident(g171,g172)
    c: Coincident(g172,g173)
    c: Coincident(g173,g174)
    c: Coincident(g174,g175)
    c: Coincident(g175,g176)
    c: Coincident(g176,g177)
    c: Coincident(g177,g178)
    c: Coincident(g178,g179)
    c: Coincident(g179,g180)
    c: Coincident(g180,g181)
    c: Coincident(g181,g182)
    c: Coincident(g182,g183)
    c: Coincident(g183,g184)
    c: Coincident(g184,g185)
    c: Coincident(g185,g186)
    c: Coincident(g186,g187)
    c: Coincident(g187,g188)
    c: Coincident(g188,g189)
    c: Coincident(g189,g190)
    c: Coincident(g190,g191)
    c: Coincident(g191,g192)
    c: Coincident(g192,g193)
    c: Coincident(g193,g194)
    c: Coincident(g194,g195)
    c: Coincident(g195,g196)
    c: Coincident(g196,g197)
    c: Coincident(g197,g198)
    c: Coincident(g198,g199)
    c: Coincident(g199,g200)
    c: Coincident(g200,g201)
    c: Coincident(g201,g202)
    c: Coincident(g202,g203)
    c: Coincident(g203,g204)
    c: Coincident(g204,g205)
    c: Coincident(g205,g206)
    c: Coincident(g206,g207)
    c: Coincident(g207,g208)
    c: Coincident(g208,g141)
    c: Coincident(g209,g210)
    c: Coincident(g210,g211)
    c: Coincident(g211,g212)
    c: Coincident(g212,g213)
    c: Coincident(g213,g214)
    c: Coincident(g214,g215)
    c: Coincident(g215,g216)
    c: Coincident(g216,g209)
    c: Coincident(g217,g218)
    c: Coincident(g218,g219)
    c: Coincident(g219,g220)
    c: Coincident(g220,g221)
    c: Coincident(g221,g222)
    c: Coincident(g222,g223)
    c: Coincident(g223,g224)
    c: Coincident(g224,g225)
    c: Coincident(g225,g226)
    c: Coincident(g226,g227)
    c: Coincident(g227,g228)
    c: Coincident(g228,g229)
    c: Coincident(g229,g230)
    c: Coincident(g230,g231)
    c: Coincident(g231,g232)
    c: Coincident(g232,g233)
    c: Coincident(g233,g234)
    c: Coincident(g234,g235)
    c: Coincident(g235,g236)
    c: Coincident(g236,g237)
    c: Coincident(g237,g238)
    c: Coincident(g238,g239)
    c: Coincident(g239,g240)
    c: Coincident(g240,g241)
    c: Coincident(g241,g242)
    c: Coincident(g242,g243)
    c: Coincident(g243,g244)
    c: Coincident(g244,g245)
    c: Coincident(g245,g246)
    c: Coincident(g246,g247)
    c: Coincident(g247,g248)
    c: Coincident(g248,g249)
    c: Coincident(g249,g250)
    c: Coincident(g250,g251)
    c: Coincident(g251,g252)
    c: Coincident(g252,g253)
    c: Coincident(g253,g254)
    c: Coincident(g254,g255)
    c: Coincident(g255,g256)
    c: Coincident(g256,g257)
    c: Coincident(g257,g258)
    c: Coincident(g258,g259)
    c: Coincident(g259,g260)
    c: Coincident(g260,g261)
    c: Coincident(g261,g262)
    c: Coincident(g262,g263)
    c: Coincident(g263,g264)
    c: Coincident(g264,g265)
    c: Coincident(g265,g266)
    c: Coincident(g266,g267)
    c: Coincident(g267,g268)
    c: Coincident(g268,g269)
    c: Coincident(g269,g270)
    c: Coincident(g270,g271)
    c: Coincident(g271,g272)
    c: Coincident(g272,g273)
    c: Coincident(g273,g274)
    c: Coincident(g274,g275)
    c: Coincident(g275,g276)
    c: Coincident(g276,g277)
    c: Coincident(g277,g278)
    c: Coincident(g278,g279)
    c: Coincident(g279,g280)
    c: Coincident(g280,g281)
    c: Coincident(g281,g282)
    c: Coincident(g282,g283)
    c: Coincident(g283,g284)
    c: Coincident(g284,g285)
    c: Coincident(g285,g286)
    c: Coincident(g286,g287)
    c: Coincident(g287,g288)
    c: Coincident(g288,g289)
    c: Coincident(g289,g290)
    c: Coincident(g290,g291)
    c: Coincident(g291,g217)
FEATURE [PartDesign::Pocket] Pocket029
  BaseFeature = -> Pad032
  Direction = (0,0,1)
  Length = 0.4
  Length2 = 5
  Profile = -> Sketch050
  ReferenceAxis = -> Sketch050 [N_Axis]
  Refine = true
  SideType = 0
  Suppressed = false
  Type = 0
  Type2 = 0
FEATURE [PartDesign::Body] Body003  label="ThumbScrew"
  AllowCompound = false
  Group = -> [Sketch012,Pad012,Sketch013,Pocket011,PolarPattern,Fillet002,Sketch015,Pocket012,Sketch050,Pad032,Pocket029]
  Origin = -> Origin003
  Tip = -> Pocket029
COMPONENT P19 — same part as P18; its construction recipe is shown at P18.
COMPONENT P20 — recipe-attached ("stand001", modeled in this document).
Construction recipe (the document's own serialized feature program — sketch geometry with constraints, then the solid features built on it; lengths are millimeters unless a unit is written):

FEATURE [Sketcher::SketchObject] Sketch029
  ArcFitTolerance = 1e-06
  AttachmentSupport = -> [XY_Plane006]
  ExternalTypes = [0]
  FullyConstrained = true
  MakeInternals = false
  MapMode = 5
  _ExternalGeoVersion = 0
  expr: Constraints[22] = Sketch001.Constraints.display_inner_length
  expr: Constraints[23] = Sketch001.Constraints.display_inner_width
  sketch-geometry (10):
    g0: LineSegment StartX=-62.65 StartY=-36.55 StartZ=0 EndX=62.65 EndY=-36.55 EndZ=0
    g1: LineSegment StartX=62.65 StartY=-36.55 StartZ=0 EndX=62.65 EndY=36.55 EndZ=0
    g2: LineSegment StartX=62.65 StartY=36.55 StartZ=0 EndX=-62.65 EndY=36.55 EndZ=0
    g3: LineSegment StartX=-62.65 StartY=36.55 StartZ=0 EndX=-62.65 EndY=-36.55 EndZ=0
    g4: GeomPoint [constr] X=0 Y=0 Z=0
    g5: LineSegment StartX=-64.65 StartY=-38.55 StartZ=0 EndX=64.65 EndY=-38.55 EndZ=0
    g6: LineSegment StartX=64.65 StartY=-38.55 StartZ=0 EndX=64.65 EndY=38.55 EndZ=0
    g7: LineSegment StartX=64.65 StartY=38.55 StartZ=0 EndX=-64.65 EndY=38.55 EndZ=0
    g8: LineSegment StartX=-64.65 StartY=38.55 StartZ=0 EndX=-64.65 EndY=-38.55 EndZ=0
    g9: GeomPoint [constr] X=0 Y=0 Z=0
  constraints (24):
    c: Coincident(g0,g1)
    c: Coincident(g1,g2)
    c: Coincident(g2,g3)
    c: Coincident(g3,g0)
    c: Horizontal(g0)
    c: Horizontal(g2)
    c: Vertical(g1)
    c: Vertical(g3)
    c: Symmetric(g2,g0,g4)
    c: Coincident(g4,g-1)
    c: Coincident(g5,g6)
    c: Coincident(g6,g7)
    c: Coincident(g7,g8)
    c: Coincident(g8,g5)
    c: Horizontal(g5)
    c: Horizontal(g7)
    c: Vertical(g6)
    c: Vertical(g8)
    c: Symmetric(g7,g5,g9)
    c: Coincident(g9,g4)
    c: DistanceY(g1,g6) = 2
    c: DistanceX(g1,g6) = 2
    c: DistanceX(g0,g0) = 125.3
    c: DistanceY(g1,g1) = 73.1
FEATURE [PartDesign::Pad] Pad015
  Direction = (0,0,1)
  Length = 15
  Length2 = 10
  Profile = -> Sketch029
  ReferenceAxis = -> Sketch029 [N_Axis]
  Refine = true
  Reversed = true
  SideType = 0
  Suppressed = false
  Type = 0
  Type2 = 0
FEATURE [Sketcher::SketchObject] Sketch030
  ArcFitTolerance = 1e-06
  AttachmentSupport = -> [XY_Plane006]
  ExternalGeometry = -> [Pad015]
  ExternalTypes = [0]
  FullyConstrained = true
  MakeInternals = false
  MapMode = 5
  _ExternalGeoVersion = 0
  sketch-geometry (10):
    g0: LineSegment StartX=-57.65 StartY=-31.55 StartZ=0 EndX=57.65 EndY=-31.55 EndZ=0
    g1: LineSegment StartX=57.65 StartY=-31.55 StartZ=0 EndX=57.65 EndY=31.55 EndZ=0
    g2: LineSegment StartX=57.65 StartY=31.55 StartZ=0 EndX=-57.65 EndY=31.55 EndZ=0
    g3: LineSegment StartX=-57.65 StartY=31.55 StartZ=0 EndX=-57.65 EndY=-31.55 EndZ=0
    g4: GeomPoint [constr] X=0 Y=0 Z=0
    g5: LineSegment StartX=-64.65 StartY=-38.55 StartZ=0 EndX=64.65 EndY=-38.55 EndZ=0
    g6: LineSegment StartX=64.65 StartY=-38.55 StartZ=0 EndX=64.65 EndY=38.55 EndZ=0
    g7: LineSegment StartX=64.65 StartY=38.55 StartZ=0 EndX=-64.65 EndY=38.55 EndZ=0
    g8: LineSegment StartX=-64.65 StartY=38.55 StartZ=0 EndX=-64.65 EndY=-38.55 EndZ=0
    g9: GeomPoint [constr] X=0 Y=0 Z=0
  constraints (23):
    c: Coincident(g0,g1)
    c: Coincident(g1,g2)
    c: Coincident(g2,g3)
    c: Coincident(g3,g0)
    c: Horizontal(g0)
    c: Horizontal(g2)
    c: Vertical(g1)
    c: Vertical(g3)
    c: Symmetric(g2,g0,g4)
    c: Coincident(g4,g-1)
    c: Coincident(g5,g6)
    c: Coincident(g7,g8)
    c: Coincident(g8,g5)
    c: Horizontal(g5)
    c: Horizontal(g7)
    c: Vertical(g6)
    c: Vertical(g8)
    c: Symmetric(g7,g5,g9)
    c: Coincident(g9,g4)
    c: DistanceX(g1,g6) = 7
    c: DistanceY(g1,g6) = 7
    c: Coincident(g7,g6)
    c: Coincident(g6,g-3)
FEATURE [PartDesign::Pad] Pad016
  BaseFeature = -> Pad015
  Direction = (0,0,1)
  Length = 2
  Length2 = 10
  Profile = -> Sketch030
  ReferenceAxis = -> Sketch030 [N_Axis]
  Refine = true
  SideType = 0
  Suppressed = false
  Type = 0
  Type2 = 0
FEATURE [Sketcher::SketchObject] Sketch031
  ArcFitTolerance = 1e-06
  AttachmentSupport = -> [Pad016]
  ExternalGeometry = -> [Pad016]
  ExternalTypes = [0]
  FullyConstrained = true
  MakeInternals = false
  MapMode = 5
  Placement = pos=(0,0,2) rot=(0,0,1;0rad)
  _ExternalGeoVersion = 0
  sketch-geometry (7):
    g0: LineSegment StartX=-64.65 StartY=38.55 StartZ=0 EndX=-64.65 EndY=23.55 EndZ=0
    g1: LineSegment StartX=-64.65 StartY=23.55 StartZ=0 EndX=-59.65 EndY=23.55 EndZ=0
    g2: LineSegment StartX=-64.65 StartY=38.55 StartZ=0 EndX=-49.65 EndY=38.55 EndZ=0
    g3: LineSegment StartX=-49.65 StartY=38.55 StartZ=0 EndX=-49.65 EndY=33.55 EndZ=0
    g4: LineSegment StartX=-59.65 StartY=23.55 StartZ=0 EndX=-59.65 EndY=30.55 EndZ=0
    g5: ArcOfCircle CenterX=-56.65 CenterY=30.55 CenterZ=0 NormalX=0 NormalY=0 NormalZ=1 AngleXU=0 Radius=3 StartAngle=1.5708 EndAngle=3.14159
    g6: LineSegment StartX=-56.65 StartY=33.55 StartZ=0 EndX=-49.65 EndY=33.55 EndZ=0
  constraints (19):
    c: Coincident(g0,g-3)
    c: Vertical(g0)
    c: Coincident(g1,g0)
    c: Horizontal(g1)
    c: Coincident(g2,g0)
    c: Horizontal(g2)
    c: Coincident(g3,g2)
    c: Vertical(g3)
    c: Equal(g2,g0)
    c: Coincident(g1,g4)
    c: Vertical(g4)
    c: Tangent(g4,g5) = 1.5708
    c: Tangent(g5,g6) = 1.5708
    c: Horizontal(g6)
    c: Coincident(g6,g3)
    c: Radius(g5) = 3
    c: DistanceY(g0,g0) = 15
    c: Equal(g3,g1)
    c: DistanceX(g1,g1) = 5
FEATURE [PartDesign::Pad] Pad017
  BaseFeature = -> Pad016
  Direction = (0,-0.3,1)
  Length = 20
  Length2 = 10
  Profile = -> Sketch031
  ReferenceAxis = -> Sketch031 [N_Axis]
  Refine = true
  SideType = 0
  Suppressed = false
  Type = 0
  Type2 = 0
  UseCustomVector = true
FEATURE [PartDesign::Mirrored] Mirrored007
  MirrorPlane = -> Sketch031 [V_Axis]
  Refine = true
  Suppressed = false
  TransformMode = 0
FEATURE [PartDesign::Mirrored] Mirrored008
  MirrorPlane = -> Sketch031 [H_Axis]
  Refine = true
  Suppressed = false
  TransformMode = 0
FEATURE [PartDesign::MultiTransform] MultiTransform002
  BaseFeature = -> Pad017
  Originals = -> [Pad017]
  Refine = true
  Suppressed = false
  TransformMode = 0
  Transformations = -> [Mirrored007,Mirrored008]
FEATURE [PartDesign::Body] Body005  label="stand"
  AllowCompound = false
  Group = -> [Sketch029,Pad015,Sketch030,Pad016,Sketch031,Pad017,MultiTransform002,Mirrored007,Mirrored008]
  Origin = -> Origin006
  Tip = -> MultiTransform002
PROVENANCE & LICENSES
A FreeCAD (.FCStd) document from a public repository crawl; recipes are the document's own serialized feature recipes (and, for linked parts, companion documents' recipes).
License: as declared in the source repository (recorded in the dataset sidecar).
